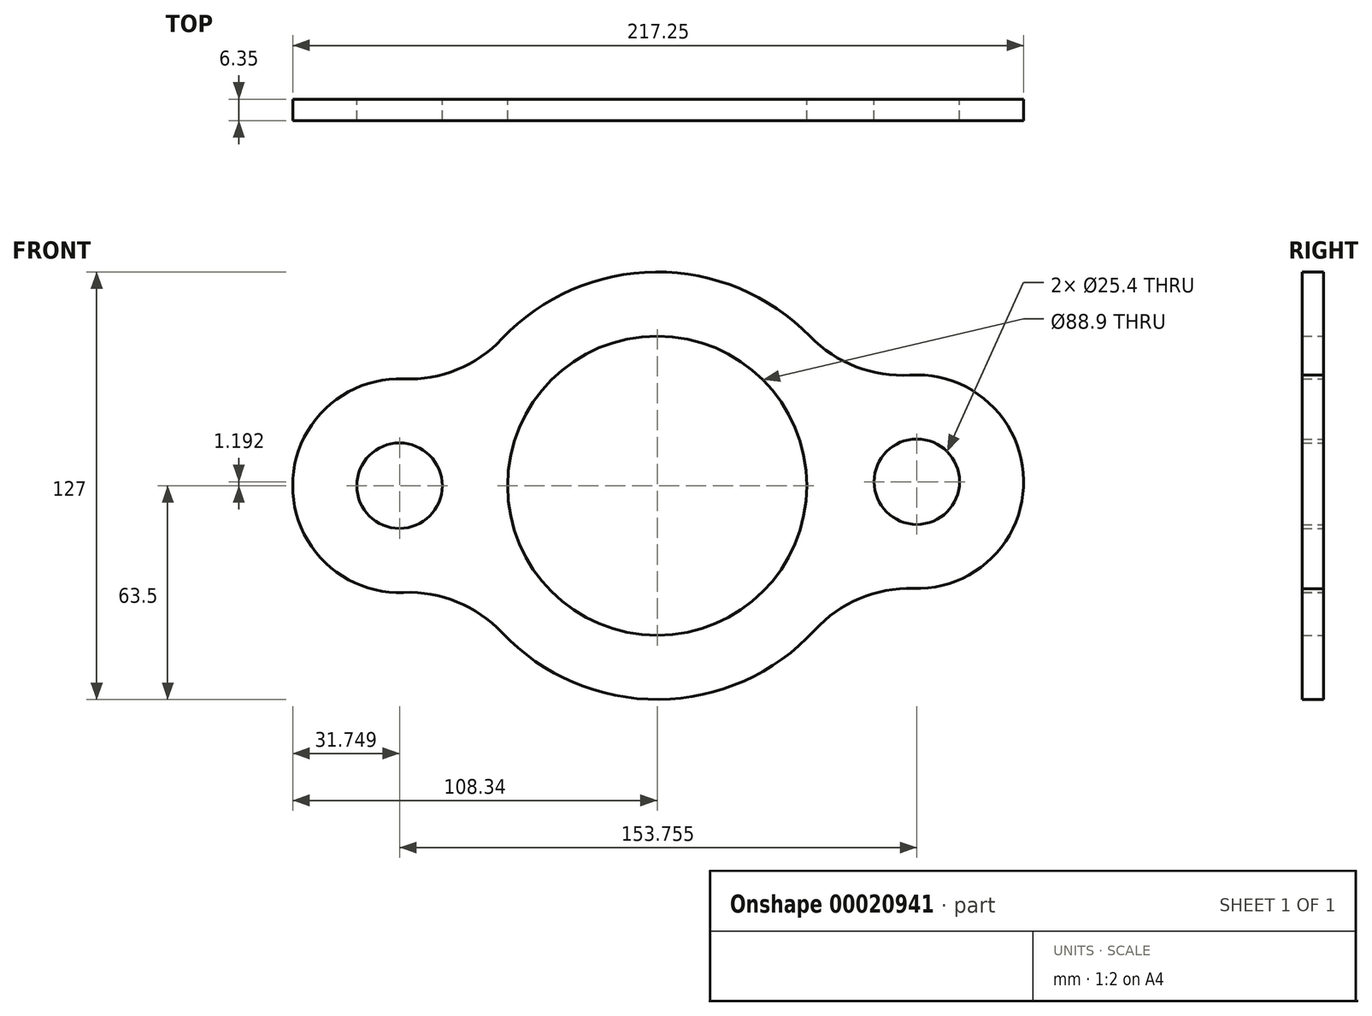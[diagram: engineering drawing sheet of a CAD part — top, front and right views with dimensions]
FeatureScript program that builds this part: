
annotation { "Feature Type Name" : "Feature", "Feature Type Description" : "" }
export const myFeature = defineFeature(function(context is Context, id is Id, definition is map)
    precondition{}
    {
        {
            var Q0;
            Q0=qCreatedBy(makeId("Front.planeOp"),FACE);
            var sketch = newSketch(context, id + "F0", { "sketchPlane" : qUnion([Q0])});
            skCircle(sketch, "E0", {"center": v(0, 0) * mm, "radius": 44.45 * mm});
            skArc(sketch, "E1", {"start": v(-46.14, -43.62) * mm, "mid": v(0.5, -63.5) * mm, "end": v(46.83, -42.89) * mm});
            skArc(sketch, "E2", {"start": v(76.15, -30.54) * mm, "mid": v(108.91, 1.68) * mm, "end": v(75.17, 32.88) * mm});
            skCircle(sketch, "E3", {"center": v(-76.6, 0) * mm, "radius": 12.7 * mm});
            skCircle(sketch, "E4", {"center": v(77.16, 1.2) * mm, "radius": 12.7 * mm});
            skArc(sketch, "E5", {"start": v(-75.34, 31.73) * mm, "mid": v(-108.34, 0) * mm, "end": v(-75.34, -31.73) * mm});
            skLineSegment(sketch, "E6", {"start": v(-76.6, 0) * mm, "end": v(89.8, 0) * mm});
            skArc(sketch, "E7.trimOffspring", {"start": v(45.48, 44.31) * mm, "mid": v(-0.48, 63.5) * mm, "end": v(-46.14, 43.62) * mm});
            skPoint(sketch, "E8.visualSharp", {"position": v(-58.04, 25.77) * mm});
            skArc(sketch, "E8.filletArc", {"start": v(-75.34, 31.73) * mm, "mid": v(-59.45, 34.51) * mm, "end": v(-46.14, 43.62) * mm});
            skPoint(sketch, "E9.visualSharp", {"position": v(-58.04, -25.77) * mm});
            skArc(sketch, "E9.filletArc", {"start": v(-46.14, -43.62) * mm, "mid": v(-59.45, -34.51) * mm, "end": v(-75.34, -31.73) * mm});
            skPoint(sketch, "E10.visualSharp", {"position": v(58.57, -24.54) * mm});
            skArc(sketch, "E10.filletArc", {"start": v(76.15, -30.54) * mm, "mid": v(60.14, -33.5) * mm, "end": v(46.83, -42.89) * mm});
            skPoint(sketch, "E11.visualSharp", {"position": v(57.78, 26.34) * mm});
            skArc(sketch, "E11.filletArc", {"start": v(45.48, 44.31) * mm, "mid": v(59.07, 35.35) * mm, "end": v(75.17, 32.88) * mm});
            skSolve(sketch);
        }
        {
            var Q0;
            Q0 = qSketchRegion(id + "F0", true);
            extrude(context, id + "F1", {"entities" : qUnion([Q0]), "depth" : 6.35 * mm});
        }
    });
